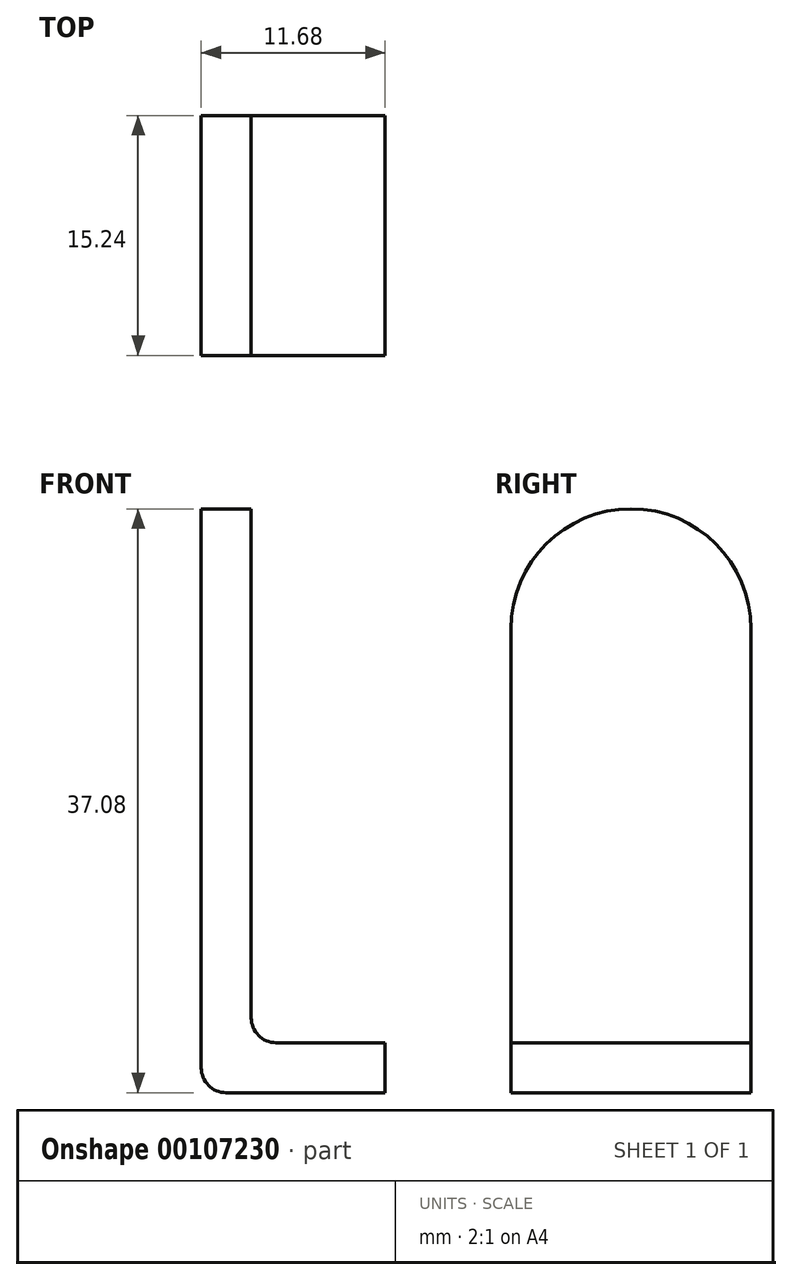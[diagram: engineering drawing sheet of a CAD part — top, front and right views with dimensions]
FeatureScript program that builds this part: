
annotation { "Feature Type Name" : "Feature", "Feature Type Description" : "" }
export const myFeature = defineFeature(function(context is Context, id is Id, definition is map)
    precondition{}
    {
        {
            var Q0;
            Q0=qCreatedBy(makeId("Front.planeOp"),FACE);
            var sketch = newSketch(context, id + "F0", { "sketchPlane" : qUnion([Q0])});
            skLineSegment(sketch, "E0", {"start": v(0, 37.08) * mm, "end": v(3.17, 37.08) * mm});
            skLineSegment(sketch, "E1", {"start": v(3.17, 37.08) * mm, "end": v(3.18, 3.18) * mm});
            skLineSegment(sketch, "E2", {"start": v(3.18, 3.18) * mm, "end": v(11.68, 3.18) * mm});
            skLineSegment(sketch, "E3", {"start": v(11.68, 3.18) * mm, "end": v(11.68, 0) * mm});
            skLineSegment(sketch, "E4", {"start": v(11.68, 0) * mm, "end": v(0, 0) * mm});
            skLineSegment(sketch, "E5", {"start": v(0, 0) * mm, "end": v(0, 37.08) * mm});
            skSolve(sketch);
        }
        {
            var Q0;
            Q0=makeQuery(id+"F0.imprint","IMPRINT",FACE,{"disambiguationData":[TD([[makeQuery(id+"F0.imprint","IMPRINT",EDGE,{"derivedFrom":sQuery(id+"F0.wireOp",EDGE,"E0")}),-1.0]])]});
            extrude(context, id + "F1", {"entities" : qUnion([Q0]), "oppositeDirection" : true, "depth" : 15.24 * mm});
        }
        {
            var Q0;
            Q0=makeQuery(id+"F1.opExtrude","SWEPT_EDGE",EDGE,{"disambiguationData":[OSD([sQuery(id+"F0.wireOp",EDGE,"E1"),sQuery(id+"F0.wireOp",EDGE,"E2")])]});
            var Q1;
            Q1=makeQuery(id+"F1.opExtrude","SWEPT_EDGE",EDGE,{"disambiguationData":[OSD([sQuery(id+"F0.wireOp",EDGE,"E4"),sQuery(id+"F0.wireOp",EDGE,"E5")])]});
            fillet(context, id + "F2", {"entities" : qUnion([Q0, Q1]), "radius" : 1.59 * mm, "tangentPropagation" : true, "allowEdgeOverflow" : false});
        }
        {
            var Q0;
            Q0=makeQuery(id+"F1.opExtrude","SWEPT_FACE",FACE,{"disambiguationData":[OSD([sQuery(id+"F0.wireOp",EDGE,"E5")])]});
            var sketch = newSketch(context, id + "F3", { "sketchPlane" : qUnion([Q0])});
            skPoint(sketch, "E6", {"position": v(-7.62, 37.08) * mm});
            skCircle(sketch, "E7", {"center": v(-7.62, 29.46) * mm, "radius": 7.62 * mm});
            skSolve(sketch);
        }
        {
            var Q0;
            {var subQ0=sQuery(id+"F3.wireOp",EDGE,"E7");var subQ1=sQuery(id+"F0.wireOp",EDGE,"E5");var subQ4=makeQuery(id+"F1.opExtrude","CAP_EDGE",EDGE,{"disambiguationData":[OSD([subQ1])],"isStart":false});var subQ5=makeQuery(id+"F3.imprint","INTERSECT",VERTEX,{"derivedFrom":[subQ4,subQ0]});Q0=makeQuery(id+"F3.imprint","IMPRINT",FACE,{"disambiguationData":[TD([[makeQuery(id+"F3.imprint","IMPRINT",EDGE,{"disambiguationData":[TD([[subQ5,1.0]])],"derivedFrom":subQ0}),-1.0]])]});}
            var Q1;
            {var subQ0=sQuery(id+"F3.wireOp",EDGE,"E7");var subQ1=sQuery(id+"F0.wireOp",EDGE,"E5");var subQ4=makeQuery(id+"F1.opExtrude","CAP_EDGE",EDGE,{"disambiguationData":[OSD([subQ1])],"isStart":true});var subQ5=makeQuery(id+"F3.imprint","INTERSECT",VERTEX,{"derivedFrom":[subQ4,subQ0]});Q1=makeQuery(id+"F3.imprint","IMPRINT",FACE,{"disambiguationData":[TD([[makeQuery(id+"F3.imprint","IMPRINT",EDGE,{"disambiguationData":[TD([[subQ5,-1.0]])],"derivedFrom":subQ0}),-1.0]])]});}
            var Q2;
            Q2=makeQuery(id+"F1.opExtrude","SWEPT_FACE",FACE,{"disambiguationData":[OSD([sQuery(id+"F0.wireOp",EDGE,"E1")])]});
            extrude(context, id + "F4", {"entities" : qUnion([Q0, Q1]), "operationType" : NewBodyOperationType.REMOVE, "endBound" : BoundingType.UP_TO_SURFACE, "oppositeDirection" : true, "endBoundEntityFace" : qUnion([Q2]), "depth" : 25.4 * mm});
        }
    });
